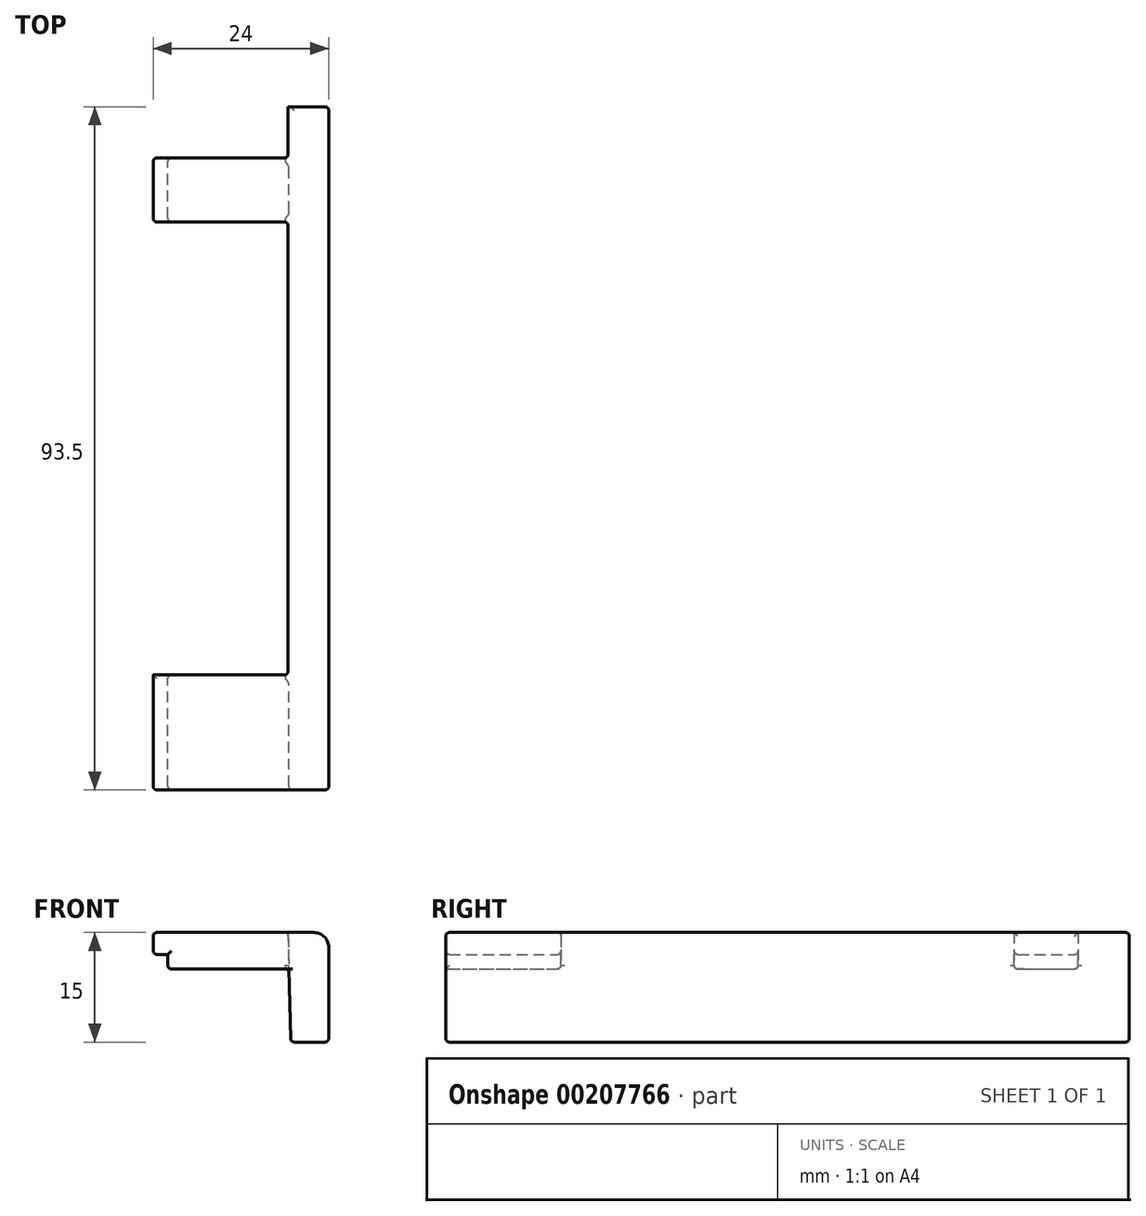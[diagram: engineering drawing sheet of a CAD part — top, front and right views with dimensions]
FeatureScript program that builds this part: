
annotation { "Feature Type Name" : "Feature", "Feature Type Description" : "" }
export const myFeature = defineFeature(function(context is Context, id is Id, definition is map)
    precondition{}
    {
        {
            var Q0;
            Q0=qCreatedBy(makeId("Front.planeOp"),FACE);
            var sketch = newSketch(context, id + "F0", { "sketchPlane" : qUnion([Q0])});
            skLineSegment(sketch, "E0", {"start": v(-5.2, 0) * mm, "end": v(0, 0) * mm});
            skLineSegment(sketch, "E1", {"start": v(0, 0) * mm, "end": v(0, 15) * mm});
            skLineSegment(sketch, "E2", {"start": v(0, 15) * mm, "end": v(-24, 15) * mm});
            skLineSegment(sketch, "E3", {"start": v(-24, 15) * mm, "end": v(-24, 12) * mm});
            skLineSegment(sketch, "E4", {"start": v(-24, 12) * mm, "end": v(-22, 12) * mm});
            skLineSegment(sketch, "E5", {"start": v(-22, 12) * mm, "end": v(-22, 10) * mm});
            skLineSegment(sketch, "E6", {"start": v(-22, 10) * mm, "end": v(-5.45, 10) * mm});
            skLineSegment(sketch, "E7", {"start": v(-5.45, 10) * mm, "end": v(-5.2, 0) * mm});
            skSolve(sketch);
        }
        {
            var Q0;
            Q0 = qSketchRegion(id + "F0", true);
            extrude(context, id + "F1", {"entities" : qUnion([Q0]), "depth" : 93.5 * mm});
        }
        {
            var Q0;
            Q0=makeQuery(id+"F1.opExtrude","SWEPT_FACE",FACE,{"disambiguationData":[OSD([sQuery(id+"F0.wireOp",EDGE,"E3")])]});
            var sketch = newSketch(context, id + "F2", { "sketchPlane" : qUnion([Q0])});
            skLineSegment(sketch, "E8.bottom", {"start": v(15.75, 15) * mm, "end": v(77.75, 15) * mm});
            skLineSegment(sketch, "E8.top", {"start": v(15.75, 0) * mm, "end": v(77.75, 0) * mm});
            skLineSegment(sketch, "E8.left", {"start": v(15.75, 15) * mm, "end": v(15.75, 0) * mm});
            skLineSegment(sketch, "E8.right", {"start": v(77.75, 15) * mm, "end": v(77.75, 0) * mm});
            skLineSegment(sketch, "E9.bottom", {"start": v(0, 15) * mm, "end": v(7, 15) * mm});
            skLineSegment(sketch, "E9.top", {"start": v(0, 0) * mm, "end": v(7, 0) * mm});
            skLineSegment(sketch, "E9.left", {"start": v(0, 15) * mm, "end": v(0, 0) * mm});
            skLineSegment(sketch, "E9.right", {"start": v(7, 15) * mm, "end": v(7, 0) * mm});
            skSolve(sketch);
        }
        {
            var Q0;
            Q0 = qSketchRegion(id + "F2", true);
            var Q1;
            Q1=makeQuery(id+"F1.opExtrude","SWEPT_FACE",FACE,{"disambiguationData":[OSD([sQuery(id+"F0.wireOp",EDGE,"E7")])]});
            extrude(context, id + "F3", {"entities" : qUnion([Q0]), "operationType" : NewBodyOperationType.REMOVE, "endBound" : BoundingType.UP_TO_SURFACE, "oppositeDirection" : true, "endBoundEntityFace" : qUnion([Q1]), "depth" : 25.4 * mm});
        }
        {
            var Q0;
            Q0=makeQuery(id+"F1.opExtrude","SWEPT_EDGE",EDGE,{"disambiguationData":[OSD([sQuery(id+"F0.wireOp",EDGE,"E1"),sQuery(id+"F0.wireOp",EDGE,"E2")])]});
            fillet(context, id + "F4", {"entities" : qUnion([Q0]), "radius" : 2 * mm, "tangentPropagation" : true, "allowEdgeOverflow" : false});
        }
        {
            var Q0;
            Q0=makeQuery(id+"F1.opExtrude","CAP_EDGE",EDGE,{"disambiguationData":[OSD([sQuery(id+"F0.wireOp",EDGE,"E2")])],"isStart":false});
            var Q1;
            Q1=makeQuery(id+"F1.opExtrude","CAP_EDGE",EDGE,{"disambiguationData":[OSD([sQuery(id+"F0.wireOp",EDGE,"E7")])],"isStart":false});
            var Q2;
            Q2=makeQuery(id+"F1.opExtrude","CAP_EDGE",EDGE,{"disambiguationData":[OSD([sQuery(id+"F0.wireOp",EDGE,"E5")])],"isStart":false});
            var Q3;
            Q3=makeQuery(id+"F1.opExtrude","CAP_EDGE",EDGE,{"disambiguationData":[OSD([sQuery(id+"F0.wireOp",EDGE,"E3")])],"isStart":false});
            var Q4;
            Q4=makeQuery(id+"F1.opExtrude","CAP_EDGE",EDGE,{"disambiguationData":[OSD([sQuery(id+"F0.wireOp",EDGE,"E4")])],"isStart":false});
            var Q5;
            Q5=makeQuery(id+"F3.boolean.opBoolean","COPY",EDGE,{"derivedFrom":makeQuery(id+"F3.opExtrude","SWEPT_EDGE",EDGE,{"disambiguationData":[OSD([sQuery(id+"F0.wireOp",EDGE,"E2"),sQuery(id+"F0.wireOp",EDGE,"E3"),sQuery(id+"F2.wireOp",EDGE,"E8.bottom"),sQuery(id+"F2.wireOp",EDGE,"E8.right")])]})});
            var Q6;
            Q6=makeQuery(id+"F3.boolean.opBoolean","COPY",EDGE,{"derivedFrom":makeQuery(id+"F3.opExtrude","CAP_EDGE",EDGE,{"disambiguationData":[OSD([sQuery(id+"F2.wireOp",EDGE,"E8.right")])],"isStart":false})});
            var Q7;
            Q7=makeQuery(id+"F3.boolean.opBoolean","COPY",EDGE,{"derivedFrom":makeQuery(id+"F3.opExtrude","CAP_EDGE",EDGE,{"disambiguationData":[OSD([sQuery(id+"F2.wireOp",EDGE,"E8.right")])],"isStart":true})});
            var Q8;
            Q8=makeQuery(id+"F3.boolean.opBoolean","INTERSECT",EDGE,{"derivedFrom":[makeQuery(id+"F1.opExtrude","SWEPT_FACE",FACE,{"disambiguationData":[OSD([sQuery(id+"F0.wireOp",EDGE,"E4")])]}),makeQuery(id+"F3.opExtrude","SWEPT_FACE",FACE,{"disambiguationData":[OSD([sQuery(id+"F2.wireOp",EDGE,"E8.right")])]})]});
            var Q9;
            Q9=makeQuery(id+"F3.boolean.opBoolean","INTERSECT",EDGE,{"derivedFrom":[makeQuery(id+"F1.opExtrude","SWEPT_FACE",FACE,{"disambiguationData":[OSD([sQuery(id+"F0.wireOp",EDGE,"E5")])]}),makeQuery(id+"F3.opExtrude","SWEPT_FACE",FACE,{"disambiguationData":[OSD([sQuery(id+"F2.wireOp",EDGE,"E8.right")])]})]});
            var Q10;
            Q10=makeQuery(id+"F3.boolean.opBoolean","INTERSECT",EDGE,{"derivedFrom":[makeQuery(id+"F1.opExtrude","SWEPT_FACE",FACE,{"disambiguationData":[OSD([sQuery(id+"F0.wireOp",EDGE,"E6")])]}),makeQuery(id+"F3.opExtrude","SWEPT_FACE",FACE,{"disambiguationData":[OSD([sQuery(id+"F2.wireOp",EDGE,"E8.right")])]})]});
            var Q11;
            Q11=makeQuery(id+"F1.opExtrude","SWEPT_EDGE",EDGE,{"disambiguationData":[OSD([sQuery(id+"F0.wireOp",EDGE,"E0"),sQuery(id+"F0.wireOp",EDGE,"E7")])]});
            var Q12;
            Q12=makeQuery(id+"F1.opExtrude","SWEPT_EDGE",EDGE,{"disambiguationData":[OSD([sQuery(id+"F0.wireOp",EDGE,"E0"),sQuery(id+"F0.wireOp",EDGE,"E1")])]});
            var Q13;
            Q13=makeQuery(id+"F1.opExtrude","CAP_EDGE",EDGE,{"disambiguationData":[OSD([sQuery(id+"F0.wireOp",EDGE,"E0")])],"isStart":true});
            var Q14;
            {var subQ0=sQuery(id+"F0.wireOp",EDGE,"E2");var subQ1=sQuery(id+"F0.wireOp",EDGE,"E1");Q14=makeQuery(id+"F4.opFillet","BLEND_EDGE",EDGE,{"blendedFrom":[makeQuery(id+"F1.opExtrude","SWEPT_EDGE",EDGE,{"disambiguationData":[OSD([subQ1,subQ0])]}),makeQuery(id+"F1.opExtrude","CAP_FACE",FACE,{"disambiguationData":[OSD([sQuery(id+"F0.wireOp",EDGE,"E0"),subQ1,subQ0,sQuery(id+"F0.wireOp",EDGE,"E3"),sQuery(id+"F0.wireOp",EDGE,"E4"),sQuery(id+"F0.wireOp",EDGE,"E5"),sQuery(id+"F0.wireOp",EDGE,"E6"),sQuery(id+"F0.wireOp",EDGE,"E7")])],"isStart":true})],"blendedInto":[makeQuery(id+"F1.opExtrude","CAP_FACE",FACE,{"disambiguationData":[OSD([sQuery(id+"F0.wireOp",EDGE,"E0"),subQ1,subQ0,sQuery(id+"F0.wireOp",EDGE,"E3"),sQuery(id+"F0.wireOp",EDGE,"E4"),sQuery(id+"F0.wireOp",EDGE,"E5"),sQuery(id+"F0.wireOp",EDGE,"E6"),sQuery(id+"F0.wireOp",EDGE,"E7")])],"isStart":true})]});}
            var Q15;
            Q15=makeQuery(id+"F3.boolean.opBoolean","MERGE",EDGE,{"derivedFrom":[makeQuery(id+"F1.opExtrude","CAP_EDGE",EDGE,{"disambiguationData":[OSD([sQuery(id+"F0.wireOp",EDGE,"E7")])],"isStart":true})],"fromTools":[makeQuery(id+"F3.opExtrude","CAP_EDGE",EDGE,{"disambiguationData":[OSD([sQuery(id+"F2.wireOp",EDGE,"E9.left")])],"isStart":false})]});
            var Q16;
            Q16=makeQuery(id+"F3.boolean.opBoolean","COPY",EDGE,{"derivedFrom":makeQuery(id+"F3.opExtrude","CAP_EDGE",EDGE,{"disambiguationData":[OSD([sQuery(id+"F2.wireOp",EDGE,"E9.right")])],"isStart":false})});
            var Q17;
            Q17=makeQuery(id+"F3.boolean.opBoolean","COPY",EDGE,{"derivedFrom":makeQuery(id+"F3.opExtrude","CAP_EDGE",EDGE,{"disambiguationData":[OSD([sQuery(id+"F2.wireOp",EDGE,"E9.bottom")])],"isStart":false})});
            var Q18;
            Q18=makeQuery(id+"F3.boolean.opBoolean","INTERSECT",EDGE,{"derivedFrom":[makeQuery(id+"F1.opExtrude","SWEPT_FACE",FACE,{"disambiguationData":[OSD([sQuery(id+"F0.wireOp",EDGE,"E6")])]}),makeQuery(id+"F3.opExtrude","SWEPT_FACE",FACE,{"disambiguationData":[OSD([sQuery(id+"F2.wireOp",EDGE,"E9.right")])]})]});
            var Q19;
            {var subQ0=sQuery(id+"F2.wireOp",EDGE,"E9.right");var subQ1=makeQuery(id+"F3.opExtrude","SWEPT_FACE",FACE,{"disambiguationData":[OSD([subQ0])]});var subQ2=sQuery(id+"F2.wireOp",EDGE,"E8.left");var subQ3=sQuery(id+"F0.wireOp",EDGE,"E7");var subQ4=sQuery(id+"F0.wireOp",EDGE,"E6");Q19=makeQuery(id+"F4.opFillet","BLEND_EDGE",EDGE,{"blendedFrom":[makeQuery(id+"F3.boolean.opBoolean","SPLIT",EDGE,{"disambiguationData":[TD([makeQuery(id+"F3.opExtrude","SWEPT_FACE",FACE,{"disambiguationData":[OSD([subQ2])]})])],"derivedFrom":makeQuery(id+"F1.opExtrude","SWEPT_EDGE",EDGE,{"disambiguationData":[OSD([subQ4,subQ3])]})}),makeQuery(id+"F3.boolean.opBoolean","COPY",FACE,{"derivedFrom":subQ1})],"blendedInto":[makeQuery(id+"F3.boolean.opBoolean","COPY",FACE,{"derivedFrom":subQ1})]});}
            var Q20;
            {var subQ0=sQuery(id+"F0.wireOp",EDGE,"E3");var subQ1=sQuery(id+"F0.wireOp",EDGE,"E4");Q20=makeQuery(id+"F3.boolean.opBoolean","SPLIT",EDGE,{"disambiguationData":[TD([makeQuery(id+"F3.opExtrude","SWEPT_FACE",FACE,{"disambiguationData":[OSD([sQuery(id+"F2.wireOp",EDGE,"E8.left")])]})])],"derivedFrom":makeQuery(id+"F1.opExtrude","SWEPT_EDGE",EDGE,{"disambiguationData":[OSD([subQ0,subQ1])]})});}
            var Q21;
            {var subQ0=sQuery(id+"F0.wireOp",EDGE,"E4");var subQ1=sQuery(id+"F0.wireOp",EDGE,"E3");Q21=makeQuery(id+"F3.boolean.opBoolean","SPLIT",EDGE,{"disambiguationData":[TD([makeQuery(id+"F3.opExtrude","SWEPT_FACE",FACE,{"disambiguationData":[OSD([sQuery(id+"F2.wireOp",EDGE,"E8.right")])]})])],"derivedFrom":makeQuery(id+"F1.opExtrude","SWEPT_EDGE",EDGE,{"disambiguationData":[OSD([subQ1,subQ0])]})});}
            var Q22;
            {var subQ0=sQuery(id+"F0.wireOp",EDGE,"E2");var subQ1=sQuery(id+"F0.wireOp",EDGE,"E3");Q22=makeQuery(id+"F3.boolean.opBoolean","SPLIT",EDGE,{"disambiguationData":[TD([makeQuery(id+"F3.opExtrude","SWEPT_FACE",FACE,{"disambiguationData":[OSD([sQuery(id+"F2.wireOp",EDGE,"E8.left")])]})])],"derivedFrom":makeQuery(id+"F1.opExtrude","SWEPT_EDGE",EDGE,{"disambiguationData":[OSD([subQ0,subQ1])]})});}
            var Q23;
            {var subQ0=sQuery(id+"F0.wireOp",EDGE,"E3");var subQ1=sQuery(id+"F0.wireOp",EDGE,"E2");Q23=makeQuery(id+"F3.boolean.opBoolean","SPLIT",EDGE,{"disambiguationData":[TD([makeQuery(id+"F3.opExtrude","SWEPT_FACE",FACE,{"disambiguationData":[OSD([sQuery(id+"F2.wireOp",EDGE,"E8.right")])]})])],"derivedFrom":makeQuery(id+"F1.opExtrude","SWEPT_EDGE",EDGE,{"disambiguationData":[OSD([subQ1,subQ0])]})});}
            var Q24;
            Q24=makeQuery(id+"F3.boolean.opBoolean","COPY",EDGE,{"derivedFrom":makeQuery(id+"F3.opExtrude","SWEPT_EDGE",EDGE,{"disambiguationData":[OSD([sQuery(id+"F0.wireOp",EDGE,"E2"),sQuery(id+"F0.wireOp",EDGE,"E3"),sQuery(id+"F2.wireOp",EDGE,"E8.bottom"),sQuery(id+"F2.wireOp",EDGE,"E8.left")])]})});
            var Q25;
            Q25=makeQuery(id+"F3.boolean.opBoolean","COPY",EDGE,{"derivedFrom":makeQuery(id+"F3.opExtrude","CAP_EDGE",EDGE,{"disambiguationData":[OSD([sQuery(id+"F2.wireOp",EDGE,"E8.left")])],"isStart":false})});
            var Q26;
            {var subQ0=sQuery(id+"F2.wireOp",EDGE,"E8.left");var subQ1=makeQuery(id+"F3.opExtrude","SWEPT_FACE",FACE,{"disambiguationData":[OSD([subQ0])]});var subQ3=sQuery(id+"F0.wireOp",EDGE,"E7");var subQ4=sQuery(id+"F0.wireOp",EDGE,"E6");Q26=makeQuery(id+"F4.opFillet","BLEND_EDGE",EDGE,{"blendedFrom":[makeQuery(id+"F3.boolean.opBoolean","SPLIT",EDGE,{"disambiguationData":[TD([subQ1])],"derivedFrom":makeQuery(id+"F1.opExtrude","SWEPT_EDGE",EDGE,{"disambiguationData":[OSD([subQ4,subQ3])]})}),makeQuery(id+"F3.boolean.opBoolean","COPY",FACE,{"derivedFrom":subQ1})],"blendedInto":[makeQuery(id+"F3.boolean.opBoolean","COPY",FACE,{"derivedFrom":subQ1})]});}
            var Q27;
            Q27=makeQuery(id+"F3.boolean.opBoolean","INTERSECT",EDGE,{"derivedFrom":[makeQuery(id+"F1.opExtrude","SWEPT_FACE",FACE,{"disambiguationData":[OSD([sQuery(id+"F0.wireOp",EDGE,"E6")])]}),makeQuery(id+"F3.opExtrude","SWEPT_FACE",FACE,{"disambiguationData":[OSD([sQuery(id+"F2.wireOp",EDGE,"E8.left")])]})]});
            var Q28;
            Q28=makeQuery(id+"F3.boolean.opBoolean","INTERSECT",EDGE,{"derivedFrom":[makeQuery(id+"F1.opExtrude","SWEPT_FACE",FACE,{"disambiguationData":[OSD([sQuery(id+"F0.wireOp",EDGE,"E5")])]}),makeQuery(id+"F3.opExtrude","SWEPT_FACE",FACE,{"disambiguationData":[OSD([sQuery(id+"F2.wireOp",EDGE,"E8.left")])]})]});
            var Q29;
            Q29=makeQuery(id+"F3.boolean.opBoolean","INTERSECT",EDGE,{"derivedFrom":[makeQuery(id+"F1.opExtrude","SWEPT_FACE",FACE,{"disambiguationData":[OSD([sQuery(id+"F0.wireOp",EDGE,"E4")])]}),makeQuery(id+"F3.opExtrude","SWEPT_FACE",FACE,{"disambiguationData":[OSD([sQuery(id+"F2.wireOp",EDGE,"E8.left")])]})]});
            var Q30;
            Q30=makeQuery(id+"F3.boolean.opBoolean","COPY",EDGE,{"derivedFrom":makeQuery(id+"F3.opExtrude","CAP_EDGE",EDGE,{"disambiguationData":[OSD([sQuery(id+"F2.wireOp",EDGE,"E8.left")])],"isStart":true})});
            var Q31;
            Q31=makeQuery(id+"F1.opExtrude","CAP_EDGE",EDGE,{"disambiguationData":[OSD([sQuery(id+"F0.wireOp",EDGE,"E0")])],"isStart":false});
            var Q32;
            Q32=makeQuery(id+"F3.boolean.opBoolean","COPY",EDGE,{"derivedFrom":makeQuery(id+"F3.opExtrude","CAP_EDGE",EDGE,{"disambiguationData":[OSD([sQuery(id+"F2.wireOp",EDGE,"E9.right")])],"isStart":true})});
            var Q33;
            Q33=makeQuery(id+"F3.boolean.opBoolean","INTERSECT",EDGE,{"derivedFrom":[makeQuery(id+"F1.opExtrude","SWEPT_FACE",FACE,{"disambiguationData":[OSD([sQuery(id+"F0.wireOp",EDGE,"E4")])]}),makeQuery(id+"F3.opExtrude","SWEPT_FACE",FACE,{"disambiguationData":[OSD([sQuery(id+"F2.wireOp",EDGE,"E9.right")])]})]});
            var Q34;
            Q34=makeQuery(id+"F3.boolean.opBoolean","INTERSECT",EDGE,{"derivedFrom":[makeQuery(id+"F1.opExtrude","SWEPT_FACE",FACE,{"disambiguationData":[OSD([sQuery(id+"F0.wireOp",EDGE,"E5")])]}),makeQuery(id+"F3.opExtrude","SWEPT_FACE",FACE,{"disambiguationData":[OSD([sQuery(id+"F2.wireOp",EDGE,"E9.right")])]})]});
            var Q35;
            {var subQ0=sQuery(id+"F0.wireOp",EDGE,"E5");var subQ1=sQuery(id+"F0.wireOp",EDGE,"E6");Q35=makeQuery(id+"F3.boolean.opBoolean","SPLIT",EDGE,{"disambiguationData":[TD([makeQuery(id+"F3.opExtrude","SWEPT_FACE",FACE,{"disambiguationData":[OSD([sQuery(id+"F2.wireOp",EDGE,"E8.left")])]})])],"derivedFrom":makeQuery(id+"F1.opExtrude","SWEPT_EDGE",EDGE,{"disambiguationData":[OSD([subQ0,subQ1])]})});}
            var Q36;
            {var subQ0=sQuery(id+"F0.wireOp",EDGE,"E6");var subQ1=sQuery(id+"F0.wireOp",EDGE,"E5");Q36=makeQuery(id+"F3.boolean.opBoolean","SPLIT",EDGE,{"disambiguationData":[TD([makeQuery(id+"F3.opExtrude","SWEPT_FACE",FACE,{"disambiguationData":[OSD([sQuery(id+"F2.wireOp",EDGE,"E8.right")])]})])],"derivedFrom":makeQuery(id+"F1.opExtrude","SWEPT_EDGE",EDGE,{"disambiguationData":[OSD([subQ1,subQ0])]})});}
            fillet(context, id + "F5", {"entities" : qUnion([Q0, Q1, Q2, Q3, Q4, Q5, Q6, Q7, Q8, Q9, Q10, Q11, Q12, Q13, Q14, Q15, Q16, Q17, Q18, Q19, Q20, Q21, Q22, Q23, Q24, Q25, Q26, Q27, Q28, Q29, Q30, Q31, Q32, Q33, Q34, Q35, Q36]), "radius" : 0.5 * mm, "tangentPropagation" : true, "allowEdgeOverflow" : false});
        }
    });
